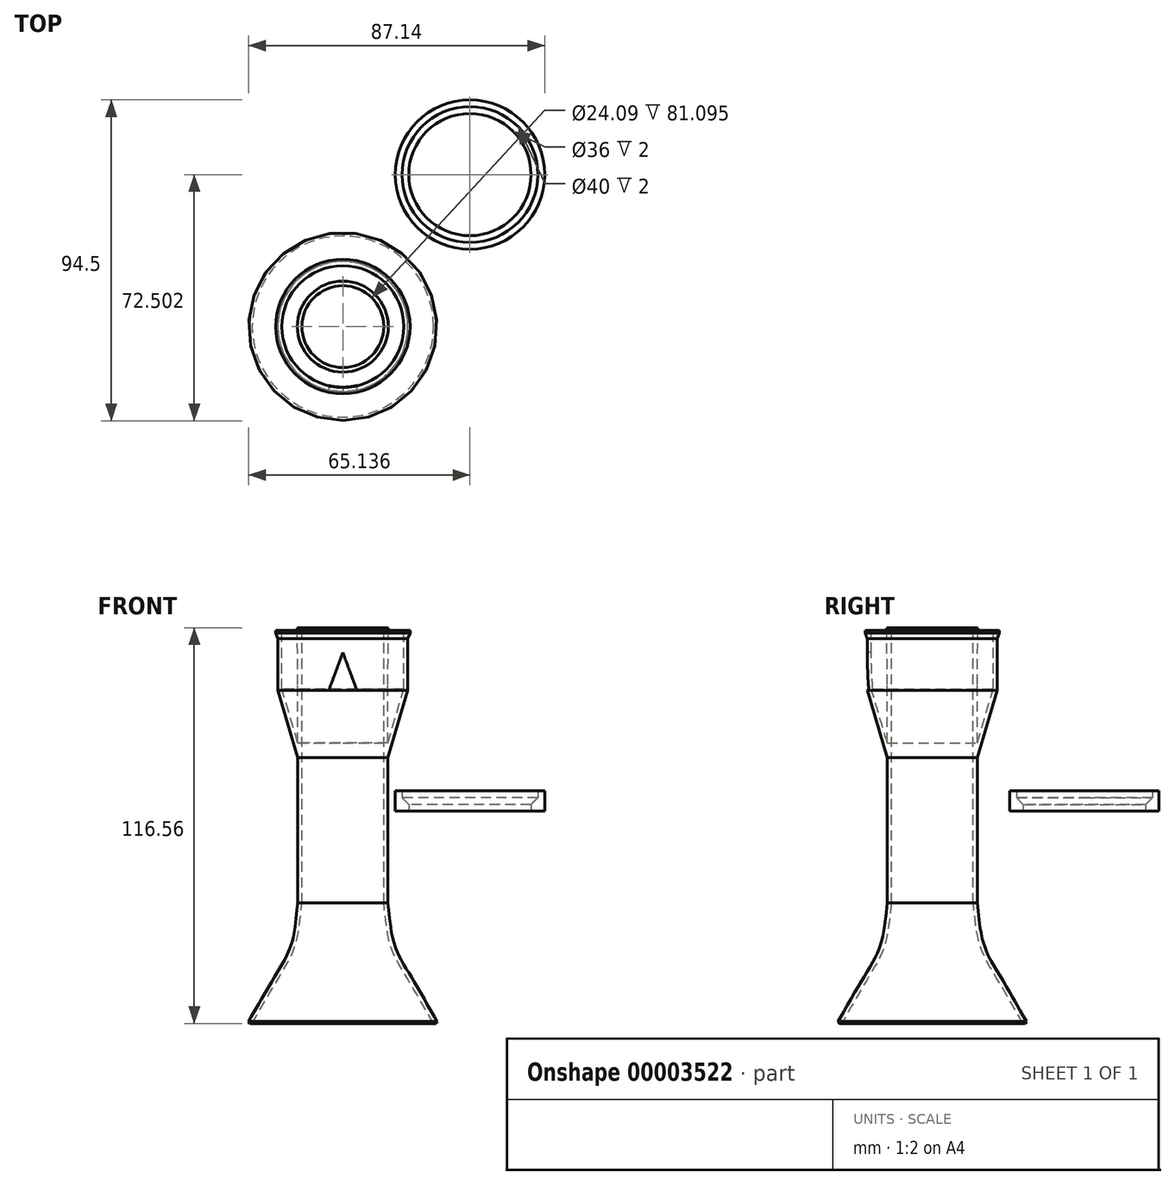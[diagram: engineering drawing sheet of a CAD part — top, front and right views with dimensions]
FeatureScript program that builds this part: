
annotation { "Feature Type Name" : "Feature", "Feature Type Description" : "" }
export const myFeature = defineFeature(function(context is Context, id is Id, definition is map)
    precondition{}
    {
        {
            var Q0;
            Q0=qCreatedBy(makeId("Right.planeOp"),FACE);
            var sketch = newSketch(context, id + "F0", { "sketchPlane" : qUnion([Q0])});
            skLineSegment(sketch, "E0.bottom", {"start": v(-15.17, 37.26) * mm, "end": v(-3.13, 37.26) * mm});
            skLineSegment(sketch, "E0.top", {"start": v(-15.17, -27.05) * mm, "end": v(-3.13, -27.05) * mm});
            skLineSegment(sketch, "E0.left", {"start": v(-15.17, 37.26) * mm, "end": v(-15.17, -27.05) * mm});
            skFitSpline(sketch, "E1", {"points": [v(-15.17, -27.05) * mm, v(-17.15, -39.49) * mm, v(-22.32, -49.58) * mm, v(-29.83, -62.52) * mm], "startDerivative": vector(-4.83, -39.42) * mm, "endDerivative": vector(-21.57, -37.45) * mm});
            skLineSegment(sketch, "E2", {"start": v(-3.13, 37.26) * mm, "end": v(-3.13, -74.65) * mm});
            skLineSegment(sketch, "E3", {"start": v(-3.13, -62.49) * mm, "end": v(-29.83, -62.52) * mm});
            skFitSpline(sketch, "E4.0", {"points": [v(-16.36, -26.9) * mm, v(-16.57, -28.57) * mm, v(-16.81, -31.04) * mm, v(-17.21, -34.2) * mm, v(-17.6, -36.46) * mm, v(-18.02, -38.25) * mm, v(-18.45, -39.6) * mm, v(-18.93, -40.93) * mm, v(-19.65, -42.54) * mm, v(-20.66, -44.46) * mm, v(-21.8, -46.4) * mm, v(-23.01, -48.4) * mm, v(-24.28, -50.52) * mm, v(-25.99, -53.43) * mm, v(-28.18, -57.24) * mm, v(-29.97, -60.36) * mm, v(-30.87, -61.92) * mm]});
            skLineSegment(sketch, "E4.1", {"start": v(-16.37, 37.25) * mm, "end": v(-16.37, -26.98) * mm});
            skLineSegment(sketch, "E5", {"start": v(-29.83, -62.52) * mm, "end": v(-30.55, -62.52) * mm});
            skLineSegment(sketch, "E6", {"start": v(-30.55, -62.52) * mm, "end": v(-30.85, -61.89) * mm});
            skLineSegment(sketch, "E7", {"start": v(-16.37, 37.25) * mm, "end": v(-15.17, 37.26) * mm});
            skLineSegment(sketch, "E8", {"start": v(-15.17, 37.26) * mm, "end": v(-15.17, 54.04) * mm});
            skLineSegment(sketch, "E9", {"start": v(-16.37, 37.25) * mm, "end": v(-16.53, 54.04) * mm});
            skLineSegment(sketch, "E10", {"start": v(-16.53, 54.04) * mm, "end": v(-15.17, 54.04) * mm});
            skLineSegment(sketch, "E11", {"start": v(-21.08, 35.98) * mm, "end": v(-21.08, 53.26) * mm});
            skLineSegment(sketch, "E12", {"start": v(-21.08, 53.26) * mm, "end": v(-22.28, 53.26) * mm});
            skLineSegment(sketch, "E13", {"start": v(-22.28, 53.26) * mm, "end": v(-22.28, 35.64) * mm});
            skLineSegment(sketch, "E14", {"start": v(-22.28, 50.79) * mm, "end": v(-22.93, 52.56) * mm});
            skLineSegment(sketch, "E15", {"start": v(-22.93, 52.56) * mm, "end": v(-22.93, 53.26) * mm});
            skLineSegment(sketch, "E16", {"start": v(-22.93, 53.26) * mm, "end": v(-22.28, 53.26) * mm});
            skLineSegment(sketch, "E17", {"start": v(-1.78, 53.26) * mm, "end": v(-16.52, 53.26) * mm, "construction": true});
            skPoint(sketch, "E18", {"position": v(-16.53, 53.26) * mm});
            skLineSegment(sketch, "E19", {"start": v(-16.52, 53.26) * mm, "end": v(-36.31, 53.26) * mm, "construction": true});
            skLineSegment(sketch, "E20", {"start": v(-16.53, 53.26) * mm, "end": v(-16.53, 54.04) * mm});
            skLineSegment(sketch, "E21", {"start": v(-15.4, 53.26) * mm, "end": v(-15.4, 54.04) * mm, "construction": true});
            skPoint(sketch, "E22.end.orphan", {"position": v(-22.28, 44.45) * mm});
            skLineSegment(sketch, "E23", {"start": v(-22.28, 35.64) * mm, "end": v(-16.37, 15.78) * mm});
            skLineSegment(sketch, "E24", {"start": v(-16.37, 15.78) * mm, "end": v(-16.37, 23.3) * mm});
            skLineSegment(sketch, "E25", {"start": v(-21.08, 43.04) * mm, "end": v(-22.28, 43.04) * mm});
            skLineSegment(sketch, "E26", {"start": v(-21.08, 35.98) * mm, "end": v(-16.37, 20.16) * mm});
            skSolve(sketch);
        }
        {
            var Q0;
            Q0=makeQuery(id+"F0.imprint","IMPRINT",FACE,{"disambiguationData":[TD([[makeQuery(id+"F0.imprint","IMPRINT",EDGE,{"derivedFrom":sQuery(id+"F0.wireOp",EDGE,"E0.left")}),-1.0]])]});
            var Q1;
            {var subQ4=sQuery(id+"F0.wireOp",EDGE,"e146de5a-5927-454d-8aab-20896795c21f");Q1=makeQuery(id+"F0.imprint","IMPRINT",FACE,{"disambiguationData":[TD([[makeQuery(id+"F0.imprint","IMPRINT",EDGE,{"derivedFrom":subQ4}),1.0]])]});}
            var Q2;
            Q2=makeQuery(id+"F0.imprint","IMPRINT",FACE,{"disambiguationData":[TD([[makeQuery(id+"F0.imprint","IMPRINT",EDGE,{"derivedFrom":sQuery(id+"F0.wireOp",EDGE,"E7")}),1.0]])]});
            var Q3;
            {var subQ1=sQuery(id+"F0.wireOp",EDGE,"E14");Q3=makeQuery(id+"F0.imprint","IMPRINT",FACE,{"disambiguationData":[TD([[makeQuery(id+"F0.imprint","IMPRINT",EDGE,{"derivedFrom":subQ1}),-1.0]])]});}
            var Q4;
            Q4=makeQuery(id+"F0.imprint","IMPRINT",FACE,{"disambiguationData":[TD([[makeQuery(id+"F0.imprint","IMPRINT",EDGE,{"derivedFrom":sQuery(id+"F0.wireOp",EDGE,"E11")}),1.0]])]});
            var Q5;
            {var subQ5=sQuery(id+"F0.wireOp",EDGE,"E23");Q5=makeQuery(id+"F0.imprint","IMPRINT",FACE,{"disambiguationData":[TD([[makeQuery(id+"F0.imprint","IMPRINT",EDGE,{"derivedFrom":subQ5}),1.0]])]});}
            var Q6;
            {var subQ4=sQuery(id+"F0.wireOp",EDGE,"E12");Q6=makeQuery(id+"F0.imprint","IMPRINT",FACE,{"disambiguationData":[TD([[makeQuery(id+"F0.imprint","IMPRINT",EDGE,{"derivedFrom":subQ4}),1.0]])]});}
            var Q7;
            Q7=sQuery(id+"F0.wireOp",EDGE,"E2");
            revolve(context, id + "F1", {"entities" : qUnion([Q0, Q1, Q2, Q3, Q4, Q5, Q6]), "axis" : qUnion([Q7]), "revolveType" : RevolveType.FULL});
        }
        {
            var Q0;
            Q0=qCreatedBy(makeId("Front.planeOp"),FACE);
            var Q1;
            Q1=sQuery(id+"F0.wireOp",VERTEX,"E14.start");
            cPlane(context, id + "F2", {"entities" : qUnion([Q0, Q1]), "cplaneType" : CPlaneType.PLANE_POINT, "offset" : 150 * mm, "width" : 150 * mm, "height" : 150 * mm});
        }
        {
            var Q0;
            Q0=qCreatedBy(id+"F2.planeOp",FACE);
            var sketch = newSketch(context, id + "F3", { "sketchPlane" : qUnion([Q0])});
            skLineSegment(sketch, "E27", {"start": v(-4.12, 35.64) * mm, "end": v(4.12, 35.64) * mm});
            skLineSegment(sketch, "E28", {"start": v(-4.12, 35.64) * mm, "end": v(0, 46.76) * mm});
            skLineSegment(sketch, "E29", {"start": v(0, 46.76) * mm, "end": v(4.12, 35.64) * mm});
            skSolve(sketch);
        }
        {
            var Q0;
            Q0=makeQuery(id+"F3.imprint","IMPRINT",FACE,{"disambiguationData":[TD([[makeQuery(id+"F3.imprint","IMPRINT",EDGE,{"derivedFrom":sQuery(id+"F3.wireOp",EDGE,"E27")}),1.0]])]});
            extrude(context, id + "F4", {"entities" : qUnion([Q0]), "operationType" : NewBodyOperationType.REMOVE, "endBound" : BoundingType.UP_TO_NEXT, "oppositeDirection" : true, "depth" : 25 * mm});
        }
        {
            var Q0;
            Q0=qCreatedBy(makeId("Top.planeOp"),FACE);
            var sketch = newSketch(context, id + "F5", { "sketchPlane" : qUnion([Q0])});
            skCircle(sketch, "E30", {"center": v(37.42, 41.65) * mm, "radius": 20 * mm});
            skPoint(sketch, "E31", {"position": v(42.87, 22.41) * mm});
            skCircle(sketch, "E32", {"center": v(37.42, 41.65) * mm, "radius": 22 * mm});
            skCircle(sketch, "E33", {"center": v(37.42, 41.65) * mm, "radius": 18 * mm});
            skSolve(sketch);
        }
        {
            var Q0;
            Q0=makeQuery(id+"F5.imprint","IMPRINT",FACE,{"disambiguationData":[TD([[makeQuery(id+"F5.imprint","IMPRINT",EDGE,{"derivedFrom":sQuery(id+"F5.wireOp",EDGE,"E30")}),1.0]])]});
            extrude(context, id + "F6", {"entities" : qUnion([Q0]), "depth" : 4 * mm});
        }
        {
            var Q0;
            Q0=makeQuery(id+"F5.imprint","IMPRINT",FACE,{"disambiguationData":[TD([[makeQuery(id+"F5.imprint","IMPRINT",EDGE,{"derivedFrom":sQuery(id+"F5.wireOp",EDGE,"E30")}),-1.0]])]});
            extrude(context, id + "F7", {"entities" : qUnion([Q0]), "operationType" : NewBodyOperationType.ADD, "depth" : 6 * mm});
        }
        {
            var Q0;
            Q0=makeQuery(id+"F6.opExtrude","CAP_EDGE",EDGE,{"disambiguationData":[OSD([sQuery(id+"F5.wireOp",EDGE,"E33")])],"isStart":false});
            chamfer(context, id + "F8", {"entities" : qUnion([Q0]), "width" : 2 * mm, "tangentPropagation" : true});
        }
    });
